# Revit family: EKF_EE_КомплектЗапасныхАксессуаровДляСоединенияКаркасовИМонтажаБоковыхИЗаднихПанелейTrivia_AVERES
name_source: partatom
category: Электрооборудование
units: mm (PartAtom-declared; Revit-internal decimal feet)

## family parameters
Всегда вертикально = Нет
На основе рабочей плоскости = Да
Общий = Да
При загрузке вырезать с полостями = Нет
Размер круглого соединителя = Использовать диаметр
Тип детали = Силовой щит
Точка расчета площади = Нет

## types (2) — shared parameters
ADSK_Единица измерения = шт.
ADSK_Завод-изготовитель = EKF
ADSK_Код изделия = AJC10
ADSK_Количество = 1
ADSK_Марка = Комплект запасных аксессуаров для соединения каркасов и монтажа боковых и задних панелей EKF AVERES
ADSK_Наименование = Комплект запасных аксессуаров для соединения каркасов и монтажа боковых и задних панелей EKF AVERES
ADSK_Обозначение = Комплект запасных аксессуаров для соединения каркасов и монтажа боковых и задних панелей EKF AVERES
t1 = 1.5 мм
Изготовитель = EKF
Отметка по умолчанию = 1219.2 мм
Серия номенклатуры = Averes
Степень защиты IP = -
ТВ = EKF_2_TRIVIA_AVERES
Тип = 654 мм
Тип установки = -
zero-valued in all types: ADSK_Масса, ADSK_Размер_Высота, ADSK_Размер_Глубина, ADSK_Размер_Ширина

## per-type parameters (varying)
| type | Выбор |
| Прямое - Комплект запасных аксессуаров для соединения каркасов и монтажа боковых и задних панелей EKF AVERES | Прямое соединение |
| Угловое - Комплект запасных аксессуаров для соединения каркасов и монтажа боковых и задних панелей EKF AVERES | Угловое соединение |
